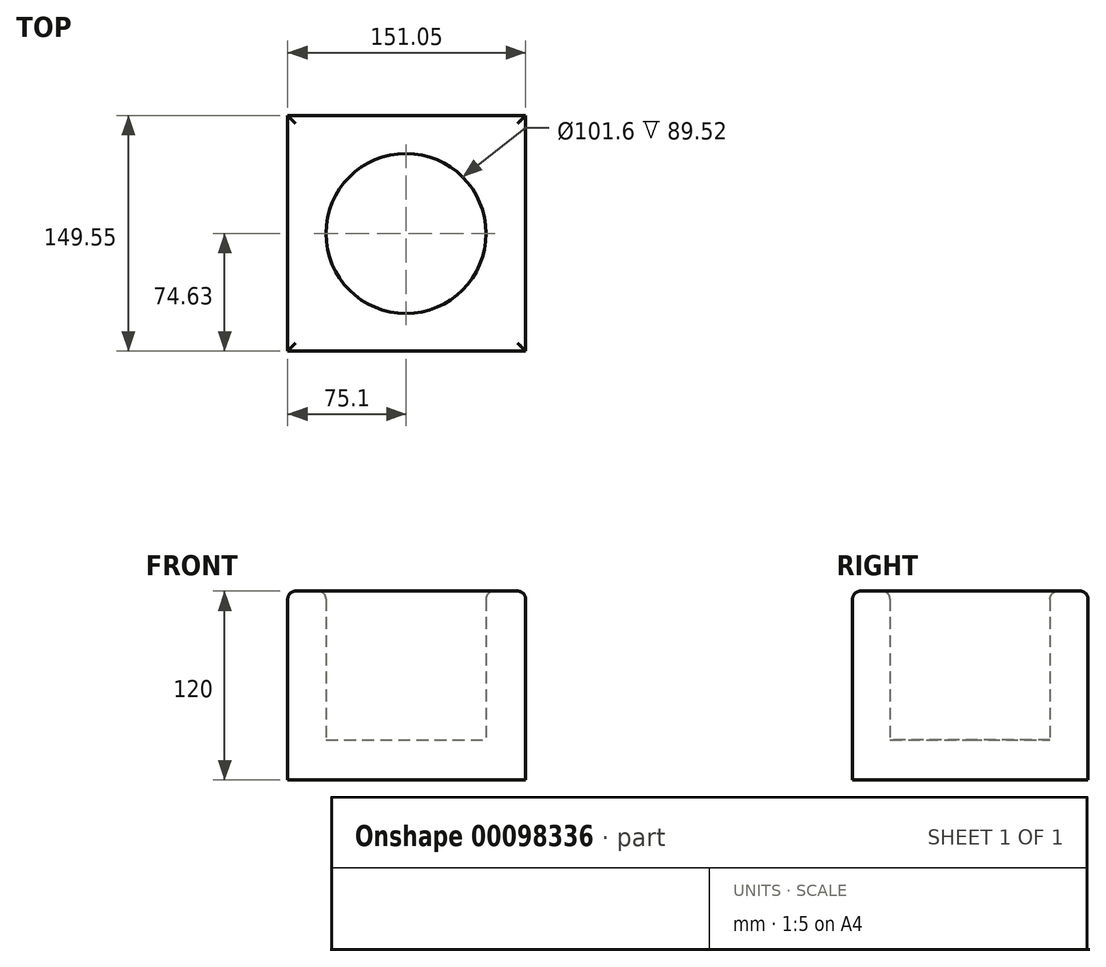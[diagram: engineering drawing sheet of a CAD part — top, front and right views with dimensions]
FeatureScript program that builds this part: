
annotation { "Feature Type Name" : "Feature", "Feature Type Description" : "" }
export const myFeature = defineFeature(function(context is Context, id is Id, definition is map)
    precondition{}
    {
        {
            var Q0;
            Q0=qCreatedBy(makeId("Top.planeOp"),FACE);
            var sketch = newSketch(context, id + "F0", { "sketchPlane" : qUnion([Q0])});
            skLineSegment(sketch, "E0.bottom", {"start": v(-75.1, -74.63) * mm, "end": v(75.95, -74.63) * mm});
            skLineSegment(sketch, "E0.top", {"start": v(-75.1, 74.92) * mm, "end": v(75.95, 74.92) * mm});
            skLineSegment(sketch, "E0.left", {"start": v(-75.1, -74.63) * mm, "end": v(-75.1, 74.92) * mm});
            skLineSegment(sketch, "E0.right", {"start": v(75.95, -74.63) * mm, "end": v(75.95, 74.92) * mm});
            skSolve(sketch);
        }
        {
            var Q0;
            Q0=makeQuery(id+"F0.imprint","IMPRINT",FACE,{"disambiguationData":[TD([[makeQuery(id+"F0.imprint","IMPRINT",EDGE,{"derivedFrom":sQuery(id+"F0.wireOp",EDGE,"E0.bottom")}),1.0]])]});
            extrude(context, id + "F1", {"entities" : qUnion([Q0]), "endBound" : BoundingType.SYMMETRIC, "depth" : 120 * mm});
        }
        {
            var Q0;
            Q0=makeQuery(id+"F1.opExtrude","CAP_FACE",FACE,{"disambiguationData":[OSD([sQuery(id+"F0.wireOp",EDGE,"E0.bottom"),sQuery(id+"F0.wireOp",EDGE,"E0.top"),sQuery(id+"F0.wireOp",EDGE,"E0.left"),sQuery(id+"F0.wireOp",EDGE,"E0.right")])],"isStart":true});
            var sketch = newSketch(context, id + "F2", { "sketchPlane" : qUnion([Q0])});
            skCircle(sketch, "E1", {"center": v(0, 0) * mm, "radius": 50.83 * mm});
            skSolve(sketch);
        }
        {
            var Q0;
            Q0=sQuery(id+"F2.wireOp",VERTEX,"E1.center");
            var Q1;
            Q1=makeQuery(id+"F1.opExtrude","SWEPT_BODY",BODY,{"disambiguationData":[OSD([sQuery(id+"F0.wireOp",EDGE,"E0.bottom"),sQuery(id+"F0.wireOp",EDGE,"E0.top"),sQuery(id+"F0.wireOp",EDGE,"E0.left"),sQuery(id+"F0.wireOp",EDGE,"E0.right")])]});
            hole(context, id + "F3", {"style" : HoleStyle.SIMPLE, "endStyle" : HoleEndStyle.THROUGH, "holeDiameter" : 101.6 * mm, "locations" : qUnion([Q0]), "scope" : qUnion([Q1]), "isTappedThrough" : true});
        }
        {
            var Q0;
            Q0=qSketchRegion(id+"F2",true);
            extrude(context, id + "F4", {"entities" : qUnion([Q0]), "operationType" : NewBodyOperationType.ADD, "oppositeDirection" : true, "depth" : 25.4 * mm});
        }
        {
            var Q0;
            Q0=qCreatedBy(makeId("Right.planeOp"),FACE);
            var sketch = newSketch(context, id + "F5", { "sketchPlane" : qUnion([Q0])});
            skLineSegment(sketch, "E2", {"start": v(0, 0) * mm, "end": v(0, 60.26) * mm});
            skSolve(sketch);
        }
        {
            var Q0;
            Q0=qCreatedBy(makeId("Right.planeOp"),FACE);
            var sketch = newSketch(context, id + "F6", { "sketchPlane" : qUnion([Q0])});
            skLineSegment(sketch, "E3", {"start": v(16.32, 0) * mm, "end": v(50.37, 59.67) * mm});
            skSolve(sketch);
        }
        {
            var Q0;
            Q0=qConstructionFilter(qBodyType(qCreatedBy(id+"F6",EDGE),BodyType.WIRE),ConstructionObject.NO);
            var Q1;
            Q1=sQuery(id+"F5.wireOp",EDGE,"E2");
            revolve(context, id + "F7", {"bodyType" : ToolBodyType.SURFACE, "surfaceEntities" : qUnion([Q0]), "axis" : qUnion([Q1]), "revolveType" : RevolveType.FULL});
        }
        {
            var Q0;
            Q0=makeQuery(id+"F1.opExtrude","CAP_FACE",FACE,{"disambiguationData":[OSD([sQuery(id+"F0.wireOp",EDGE,"E0.bottom"),sQuery(id+"F0.wireOp",EDGE,"E0.top"),sQuery(id+"F0.wireOp",EDGE,"E0.left"),sQuery(id+"F0.wireOp",EDGE,"E0.right")])],"isStart":false});
            fillet(context, id + "F8", {"entities" : qUnion([Q0]), "radius" : 5.08 * mm, "tangentPropagation" : true, "allowEdgeOverflow" : false});
        }
    });
